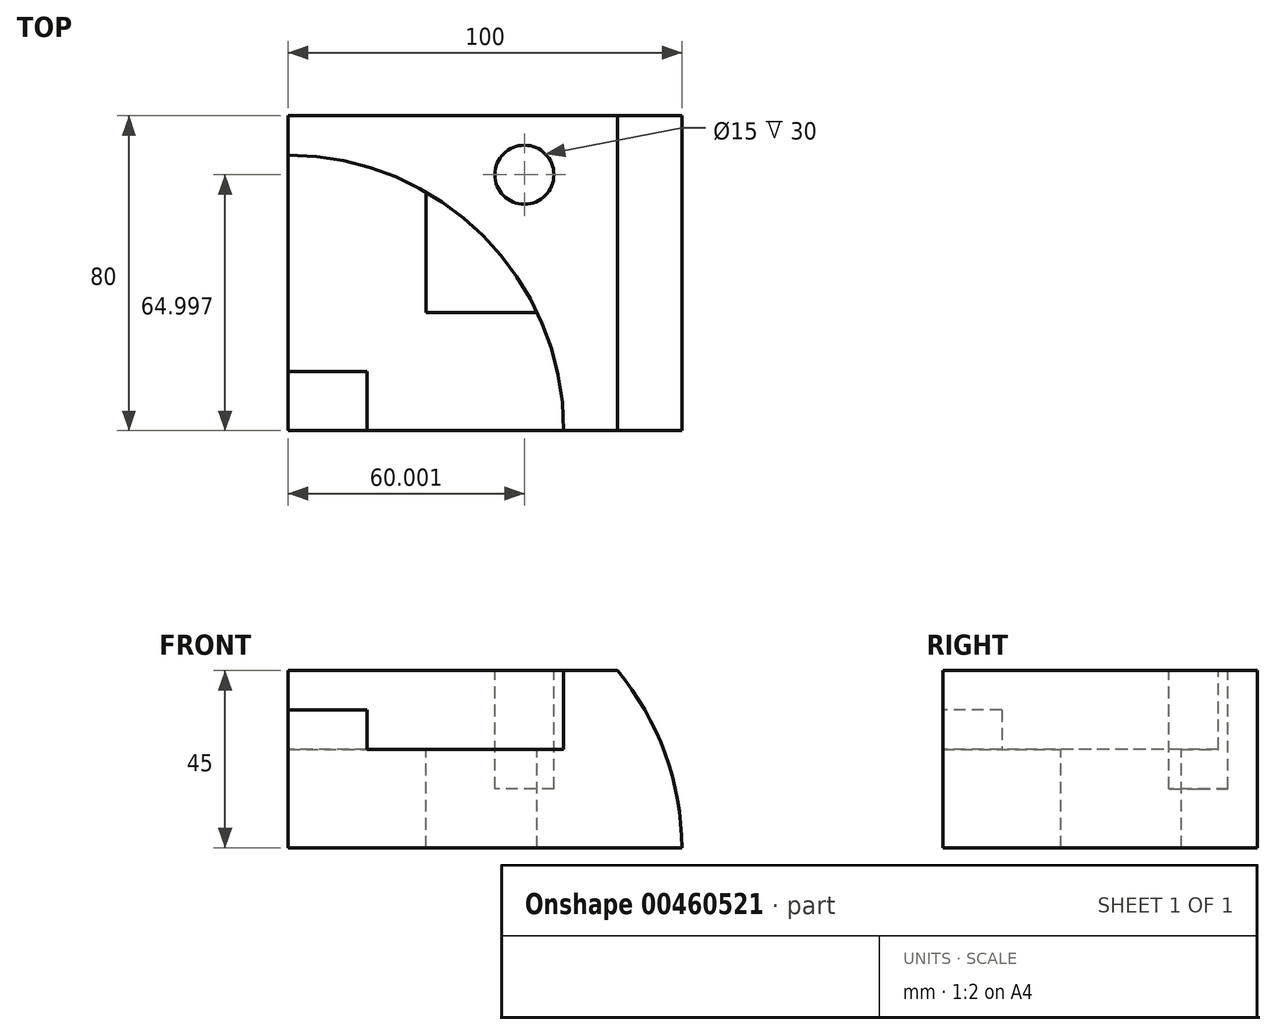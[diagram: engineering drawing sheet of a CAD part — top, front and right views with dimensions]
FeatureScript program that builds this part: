
annotation { "Feature Type Name" : "Feature", "Feature Type Description" : "" }
export const myFeature = defineFeature(function(context is Context, id is Id, definition is map)
    precondition{}
    {
        {
            var Q0;
            Q0=qCreatedBy(makeId("Top.planeOp"),FACE);
            var sketch = newSketch(context, id + "F0", { "sketchPlane" : qUnion([Q0])});
            skLineSegment(sketch, "E0.bottom", {"start": v(-51.53, 46.1) * mm, "end": v(48.47, 46.1) * mm});
            skLineSegment(sketch, "E0.top", {"start": v(-51.53, -33.9) * mm, "end": v(48.47, -33.9) * mm});
            skLineSegment(sketch, "E0.left", {"start": v(-51.53, 46.1) * mm, "end": v(-51.53, -33.9) * mm});
            skLineSegment(sketch, "E0.right", {"start": v(48.47, 46.1) * mm, "end": v(48.47, -33.9) * mm});
            skSolve(sketch);
        }
        {
            var Q0;
            Q0 = qSketchRegion(id + "F0", true);
            extrude(context, id + "F1", {"entities" : qUnion([Q0]), "depth" : 45 * mm});
        }
        {
            var Q0;
            Q0=makeQuery(id+"F1.opExtrude","CAP_FACE",FACE,{"disambiguationData":[OSD([sQuery(id+"F0.wireOp",EDGE,"E0.bottom"),sQuery(id+"F0.wireOp",EDGE,"E0.top"),sQuery(id+"F0.wireOp",EDGE,"E0.left"),sQuery(id+"F0.wireOp",EDGE,"E0.right")])],"isStart":false});
            var sketch = newSketch(context, id + "F2", { "sketchPlane" : qUnion([Q0])});
            skSolve(sketch);
        }
        {
            var Q0;
            Q0=makeQuery(id+"F1.opExtrude","SWEPT_FACE",FACE,{"disambiguationData":[OSD([sQuery(id+"F0.wireOp",EDGE,"E0.top")])]});
            var sketch = newSketch(context, id + "F3", { "sketchPlane" : qUnion([Q0])});
            skLineSegment(sketch, "E1.bottom", {"start": v(-51.53, 35) * mm, "end": v(-31.53, 35) * mm});
            skLineSegment(sketch, "E1.top", {"start": v(-51.53, 25) * mm, "end": v(-31.53, 25) * mm});
            skLineSegment(sketch, "E1.left", {"start": v(-51.53, 35) * mm, "end": v(-51.53, 25) * mm});
            skLineSegment(sketch, "E1.right", {"start": v(-31.53, 35) * mm, "end": v(-31.53, 25) * mm});
            skSolve(sketch);
        }
        {
            var Q0;
            Q0=makeQuery(id+"F2.imprint","IMPRINT",FACE,{"disambiguationData":[TD([[makeQuery(id+"F2.imprint","IMPRINT",EDGE,{"derivedFrom":makeQuery(id+"F1.opExtrude","CAP_EDGE",EDGE,{"disambiguationData":[OSD([sQuery(id+"F0.wireOp",EDGE,"E0.bottom")])],"isStart":false})}),-1.0]])]});
            var sketch = newSketch(context, id + "F4", { "sketchPlane" : qUnion([Q0])});
            skLineSegment(sketch, "E2.bottom", {"start": v(-16.53, 36.3) * mm, "end": v(14.27, 36.3) * mm});
            skLineSegment(sketch, "E2.top", {"start": v(-16.53, -3.9) * mm, "end": v(14.27, -3.9) * mm});
            skLineSegment(sketch, "E2.left", {"start": v(-16.53, 36.3) * mm, "end": v(-16.53, -3.9) * mm});
            skLineSegment(sketch, "E2.right", {"start": v(14.27, 36.3) * mm, "end": v(14.27, -3.9) * mm});
            skCircle(sketch, "E3", {"center": v(-51.53, -33.9) * mm, "radius": 70 * mm});
            skSolve(sketch);
        }
        {
            var Q0;
            {var subQ0=sQuery(id+"F4.wireOp",EDGE,"E2.left");var subQ1=sQuery(id+"F4.wireOp",EDGE,"E2.top");var subQ2=makeQuery(id+"F4.imprint","INTERSECT",VERTEX,{"derivedFrom":[subQ1,subQ0]});Q0=makeQuery(id+"F4.imprint","IMPRINT",FACE,{"disambiguationData":[TD([[makeQuery(id+"F4.imprint","IMPRINT",EDGE,{"disambiguationData":[TD([[subQ2,-1.0]])],"derivedFrom":subQ1}),1.0]])]});}
            extrude(context, id + "F5", {"entities" : qUnion([Q0]), "operationType" : NewBodyOperationType.REMOVE, "oppositeDirection" : true, "depth" : 45 * mm});
        }
        {
            var Q0;
            Q0=makeQuery(id+"F2.imprint","IMPRINT",FACE,{"disambiguationData":[TD([[makeQuery(id+"F2.imprint","IMPRINT",EDGE,{"derivedFrom":makeQuery(id+"F1.opExtrude","CAP_EDGE",EDGE,{"disambiguationData":[OSD([sQuery(id+"F0.wireOp",EDGE,"E0.bottom")])],"isStart":false})}),-1.0]])]});
            var sketch = newSketch(context, id + "F6", { "sketchPlane" : qUnion([Q0])});
            skCircle(sketch, "E4", {"center": v(8.47, 31.1) * mm, "radius": 7.5 * mm});
            skSolve(sketch);
        }
        {
            var Q0;
            Q0=qCreatedBy(makeId("Top.planeOp"),FACE);
            cPlane(context, id + "F7", {"entities" : qUnion([Q0]), "cplaneType" : CPlaneType.OFFSET, "offset" : 15 * mm, "width" : 150 * mm, "height" : 150 * mm});
        }
        {
            var Q0;
            Q0 = qSketchRegion(id + "F6", true);
            var Q1;
            Q1=qCreatedBy(id+"F7.planeOp",FACE);
            extrude(context, id + "F8", {"entities" : qUnion([Q0]), "operationType" : NewBodyOperationType.REMOVE, "endBound" : BoundingType.UP_TO_SURFACE, "oppositeDirection" : true, "endBoundEntityFace" : qUnion([Q1]), "depth" : 30 * mm});
        }
        {
            var Q0;
            {var subQ1=sQuery(id+"F4.wireOp",EDGE,"E2.left");var subQ5=sQuery(id+"F4.wireOp",EDGE,"E2.top");var subQ6=makeQuery(id+"F4.imprint","INTERSECT",VERTEX,{"derivedFrom":[subQ5,subQ1]});Q0=makeQuery(id+"F4.imprint","IMPRINT",FACE,{"disambiguationData":[TD([[makeQuery(id+"F4.imprint","IMPRINT",EDGE,{"disambiguationData":[TD([[subQ6,-1.0]])],"derivedFrom":subQ5}),-1.0]])]});}
            extrude(context, id + "F9", {"entities" : qUnion([Q0]), "operationType" : NewBodyOperationType.REMOVE, "oppositeDirection" : true, "depth" : 20 * mm});
        }
        {
            var Q0;
            Q0=makeQuery(id+"F3.imprint","IMPRINT",FACE,{"disambiguationData":[TD([[makeQuery(id+"F3.imprint","IMPRINT",EDGE,{"derivedFrom":sQuery(id+"F3.wireOp",EDGE,"E1.bottom")}),-1.0]])]});
            extrude(context, id + "F10", {"entities" : qUnion([Q0]), "operationType" : NewBodyOperationType.ADD, "oppositeDirection" : true, "depth" : 15 * mm});
        }
        {
            var Q0;
            Q0=makeQuery(id+"F10.boolean.opBoolean","MERGE",FACE,{"derivedFrom":[makeQuery(id+"F1.opExtrude","SWEPT_FACE",FACE,{"disambiguationData":[OSD([sQuery(id+"F0.wireOp",EDGE,"E0.top")])]}),makeQuery(id+"F10.opExtrude","CAP_FACE",FACE,{"disambiguationData":[OSD([sQuery(id+"F3.wireOp",EDGE,"E1.bottom"),sQuery(id+"F3.wireOp",EDGE,"E1.top"),sQuery(id+"F3.wireOp",EDGE,"E1.left"),sQuery(id+"F3.wireOp",EDGE,"E1.right")])],"isStart":true})]});
            var sketch = newSketch(context, id + "F11", { "sketchPlane" : qUnion([Q0])});
            skCircle(sketch, "E5", {"center": v(-21.53, 0) * mm, "radius": 70 * mm});
            skSolve(sketch);
        }
        {
            var Q0;
            {var subQ1=sQuery(id+"F0.wireOp",EDGE,"E0.top");var subQ2=makeQuery(id+"F1.opExtrude","SWEPT_EDGE",EDGE,{"disambiguationData":[OSD([subQ1,sQuery(id+"F0.wireOp",EDGE,"E0.right")])]});Q0=makeQuery(id+"F11.imprint","IMPRINT",FACE,{"disambiguationData":[TD([[makeQuery(id+"F11.imprint","IMPRINT",EDGE,{"derivedFrom":subQ2}),-1.0]])]});}
            extrude(context, id + "F12", {"entities" : qUnion([Q0]), "operationType" : NewBodyOperationType.REMOVE, "endBound" : BoundingType.UP_TO_NEXT, "oppositeDirection" : true, "depth" : 25 * mm});
        }
    });
